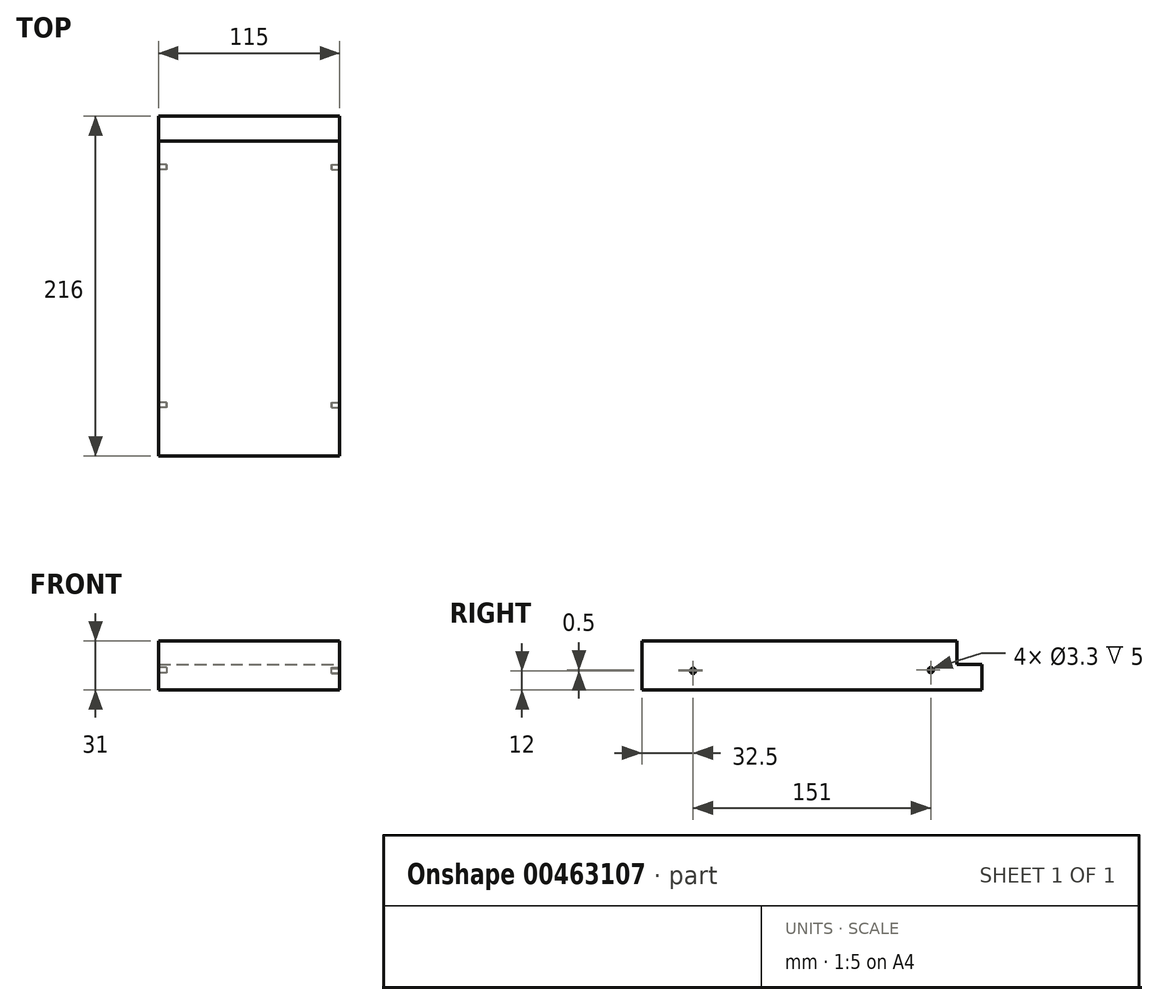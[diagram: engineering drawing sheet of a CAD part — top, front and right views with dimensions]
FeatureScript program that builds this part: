
annotation { "Feature Type Name" : "Feature", "Feature Type Description" : "" }
export const myFeature = defineFeature(function(context is Context, id is Id, definition is map)
    precondition{}
    {
        {
            var Q0;
            Q0=qCreatedBy(makeId("Top.planeOp"),FACE);
            var sketch = newSketch(context, id + "F0", { "sketchPlane" : qUnion([Q0])});
            skLineSegment(sketch, "E0.bottom", {"start": v(57.5, -108) * mm, "end": v(-57.5, -108) * mm});
            skLineSegment(sketch, "E0.top", {"start": v(57.5, 108) * mm, "end": v(-57.5, 108) * mm});
            skLineSegment(sketch, "E0.left", {"start": v(57.5, -108) * mm, "end": v(57.5, 108) * mm});
            skLineSegment(sketch, "E0.right", {"start": v(-57.5, -108) * mm, "end": v(-57.5, 108) * mm});
            skPoint(sketch, "E0.middle", {"position": v(0, 0) * mm});
            skSolve(sketch);
        }
        {
            var Q0;
            Q0 = qSketchRegion(id + "F0", true);
            extrude(context, id + "F1", {"entities" : qUnion([Q0]), "depth" : 31 * mm});
        }
        {
            var Q0;
            Q0=makeQuery(id+"F1.opExtrude","CAP_FACE",FACE,{"disambiguationData":[OSD([sQuery(id+"F0.wireOp",EDGE,"E0.bottom"),sQuery(id+"F0.wireOp",EDGE,"E0.top"),sQuery(id+"F0.wireOp",EDGE,"E0.left"),sQuery(id+"F0.wireOp",EDGE,"E0.right")])],"isStart":false});
            cPlane(context, id + "F2", {"entities" : qUnion([Q0]), "cplaneType" : CPlaneType.OFFSET, "offset" : 0 * mm, "width" : 150 * mm, "height" : 150 * mm});
        }
        {
            var Q0;
            Q0=qCreatedBy(id+"F2.planeOp",FACE);
            var sketch = newSketch(context, id + "F3", { "sketchPlane" : qUnion([Q0])});
            skLineSegment(sketch, "E1.0", {"start": v(57.5, 108) * mm, "end": v(-57.5, 108) * mm, "construction": true});
            skLineSegment(sketch, "E2.0", {"start": v(-57.5, -108) * mm, "end": v(-57.5, 108) * mm, "construction": true});
            skLineSegment(sketch, "E3.0", {"start": v(57.5, -108) * mm, "end": v(57.5, 108) * mm, "construction": true});
            skLineSegment(sketch, "E4.bottom", {"start": v(-57.5, 108) * mm, "end": v(57.5, 108) * mm});
            skLineSegment(sketch, "E4.top", {"start": v(-57.5, 92) * mm, "end": v(57.5, 92) * mm});
            skLineSegment(sketch, "E4.left", {"start": v(-57.5, 108) * mm, "end": v(-57.5, 92) * mm});
            skLineSegment(sketch, "E4.right", {"start": v(57.5, 108) * mm, "end": v(57.5, 92) * mm});
            skSolve(sketch);
        }
        {
            var Q0;
            Q0 = qSketchRegion(id + "F3", true);
            extrude(context, id + "F4", {"entities" : qUnion([Q0]), "operationType" : NewBodyOperationType.REMOVE, "oppositeDirection" : true, "depth" : 15 * mm});
        }
        {
            var Q0;
            Q0=makeQuery(id+"F1.opExtrude","SWEPT_FACE",FACE,{"disambiguationData":[OSD([sQuery(id+"F0.wireOp",EDGE,"E0.left")])]});
            cPlane(context, id + "F5", {"entities" : qUnion([Q0]), "cplaneType" : CPlaneType.OFFSET, "offset" : 0 * mm, "width" : 150 * mm, "height" : 150 * mm});
        }
        {
            var Q0;
            Q0=qCreatedBy(id+"F5.planeOp",FACE);
            var sketch = newSketch(context, id + "F6", { "sketchPlane" : qUnion([Q0])});
            skCircle(sketch, "E5", {"center": v(-75.5, 12) * mm, "radius": 1.65 * mm});
            skCircle(sketch, "E6", {"center": v(75.5, 12.5) * mm, "radius": 1.65 * mm});
            skSolve(sketch);
        }
        {
            var Q0;
            Q0 = qSketchRegion(id + "F6", true);
            extrude(context, id + "F7", {"entities" : qUnion([Q0]), "operationType" : NewBodyOperationType.REMOVE, "oppositeDirection" : true, "depth" : 5 * mm});
        }
        {
            var Q0;
            Q0=makeQuery(id+"F1.opExtrude","SWEPT_FACE",FACE,{"disambiguationData":[OSD([sQuery(id+"F0.wireOp",EDGE,"E0.right")])]});
            cPlane(context, id + "F8", {"entities" : qUnion([Q0]), "cplaneType" : CPlaneType.OFFSET, "offset" : 0 * mm, "width" : 150 * mm, "height" : 150 * mm});
        }
        {
            var Q0;
            Q0=qCreatedBy(id+"F8.planeOp",FACE);
            var sketch = newSketch(context, id + "F9", { "sketchPlane" : qUnion([Q0])});
            skCircle(sketch, "E7", {"center": v(75.5, 12.5) * mm, "radius": 1.65 * mm});
            skCircle(sketch, "E8", {"center": v(-75.5, 12.5) * mm, "radius": 1.65 * mm});
            skSolve(sketch);
        }
        {
            var Q0;
            Q0 = qSketchRegion(id + "F9", true);
            extrude(context, id + "F10", {"entities" : qUnion([Q0]), "operationType" : NewBodyOperationType.REMOVE, "oppositeDirection" : true, "depth" : 5 * mm});
        }
    });
